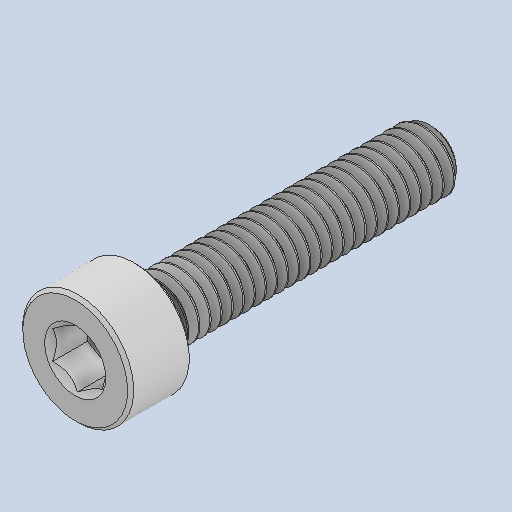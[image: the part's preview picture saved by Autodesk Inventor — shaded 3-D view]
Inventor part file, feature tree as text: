
AUTODESK INVENTOR PART (.ipt)
format: ipt  version: 2025 (Build 290162000, 162)  size: 702,464 bytes
history: native  units: in
note: dims shown in document units (in); Inventor stores cm internally (conversion verified against a paired STEP export)
features: revolve x1
ambient origin geometry x8: Origin, YZ Plane, XZ Plane, XY Plane, X Axis, Y Axis, Z Axis, Center Point
bodies: Solid1 (feature_tree)
feature tree (1):
  revolve  "Revolve2"  [1 undecoded]
note: 1 required parameter value undecoded (feature->parameter linkage not recoverable at this tier; creation-order binding heuristic only, values carry confidence <= 0.55)
